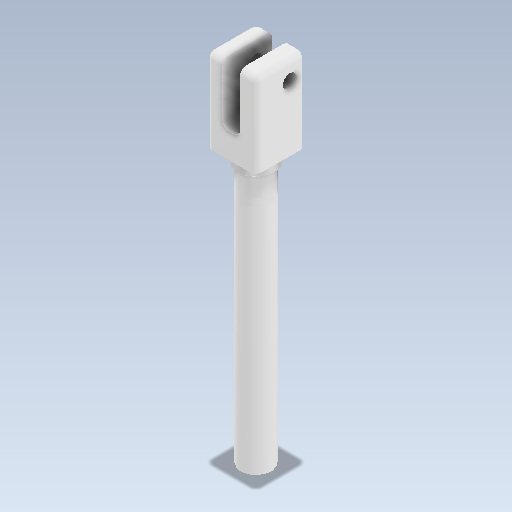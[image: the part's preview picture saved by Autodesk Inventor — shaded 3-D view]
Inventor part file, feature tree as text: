
AUTODESK INVENTOR PART (.ipt)
format: ipt  version: 2021 (Build 250183000, 183)  size: 285,184 bytes
history: native  units: mm
features: sketch x9, extrude x8, fillet x4, other x1, revolve x1, plane x1
ambient origin geometry x8: Origin, YZ Plane, XZ Plane, XY Plane, X Axis, Y Axis, Z Axis, Center Point
bodies: Body1 (feature_tree)
feature tree (24):
  other  "Sólido1"
  extrude  "Extrusión1"  Depth=5.0mm
  fillet  "Empalme1"  Radius=5.0mm
  extrude  "Extrusión2"  Depth=181.05mm
  extrude  "Extrusión3"  Depth=8.0mm
  fillet  "Empalme4"  Radius=1.0mm
  sketch  "Boceto11"  dims[d19=16.0mm d20=0.0mm d27=1.5mm d28=3.0mm d29=3.0mm d30=8.0mm d31=0.5mm d32=2.373201mm d33=90.0deg d34=1.5mm d35=3.0mm d36=5.0mm d37=1.0mm d38=7.0mm d39=2.0mm d40=7.0mm d41=0.0mm d45=1.5mm d46=1.0mm d49=2.0mm d50=32.0mm d51=32.0mm d52=362.1mm d53=0.0mm d55=2.0mm d56=5.0mm d57=44.0mm d58=0.0mm d59=6.0mm d60=2.0mm d61=0.0mm d62=1.0mm d63=1.0mm d66=6.0mm d67=181.05mm d68=6.45mm d69=5.45mm d70=2.3mm d72=0.0mm d73=0.0mm d77=177.05mm d78=0.0mm d79=0.0mm d80=0.0mm d44=0.5mm d47=0.872665mm]
  extrude  "Extrusión9"  Depth=8.0mm
  revolve  "Revolución1"  [1 undecoded]
  extrude  "Extrusión5"  TaperAngle=30.0deg  [1 undecoded]
  fillet  "Empalme2"  Radius=2.5mm
  plane  "Plano de trabajo2"
  extrude  "Extrusión6"  Depth=9.6mm
  extrude  "Extrusión7"  Depth=1.4mm
  extrude  "Extrusión8"  TaperAngle=0.0deg  [1 undecoded]
  fillet  "Empalme3"  Radius=1.5mm
  sketch  "Boceto1"  dims[d0=10.0mm d1=6.0mm d2=5.0mm]
  sketch  "Boceto2"  dims[d3=181.05mm d4=6.45mm]
  sketch  "Boceto3"  dims[d5=3.15mm d6=8.0mm d7=1.0mm]
  sketch  "Boceto6"  dims[d8=1.0mm d9=8.0mm]
  sketch  "Boceto7"  dims[d10=0.0mm d11=1.0mm]
  sketch  "Boceto8"  dims[d12=11.0mm d13=30.0deg d14=2.5mm]
  sketch  "Boceto9"  dims[d15=0.0mm d16=9.6mm]
  sketch  "Boceto10"  dims[d17=1.4mm d18=1.4mm]
note: 3 required parameter values undecoded (feature->parameter linkage not recoverable at this tier; creation-order binding heuristic only, values carry confidence <= 0.55)